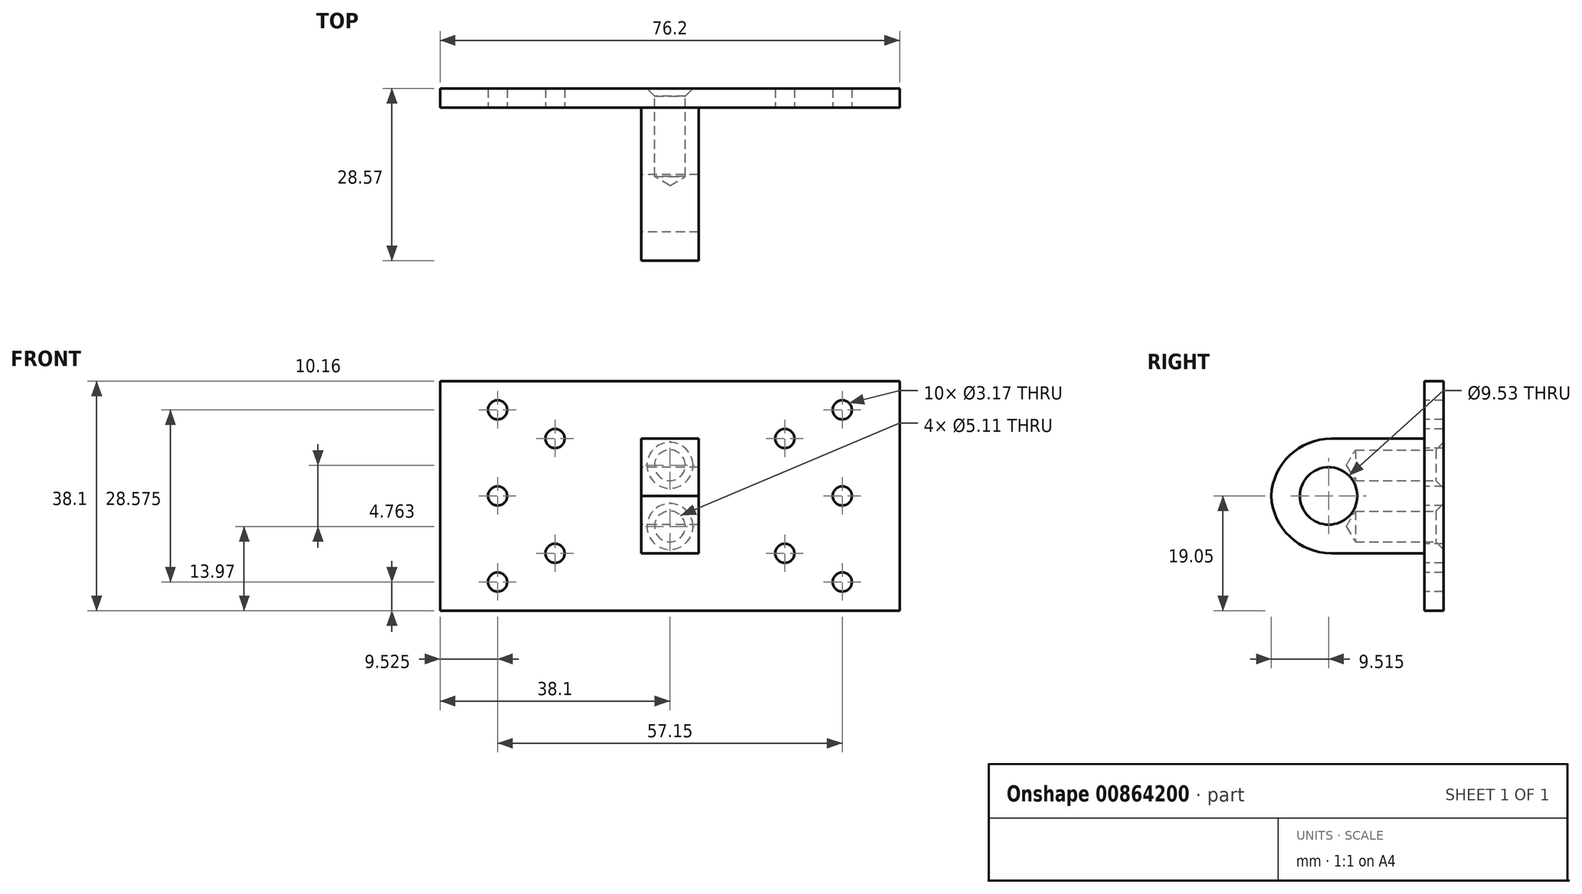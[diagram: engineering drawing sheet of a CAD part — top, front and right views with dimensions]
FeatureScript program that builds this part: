
annotation { "Feature Type Name" : "Feature", "Feature Type Description" : "" }
export const myFeature = defineFeature(function(context is Context, id is Id, definition is map)
    precondition{}
    {
        {
            var Q0;
            Q0=qCreatedBy(makeId("Right.planeOp"),FACE);
            var sketch = newSketch(context, id + "F0", { "sketchPlane" : qUnion([Q0])});
            skLineSegment(sketch, "E0.bottom", {"start": v(-12.7, 9.52) * mm, "end": v(12.7, 9.52) * mm});
            skLineSegment(sketch, "E0.top", {"start": v(-12.7, -9.53) * mm, "end": v(12.7, -9.53) * mm});
            skLineSegment(sketch, "E0.left", {"start": v(-12.7, 9.52) * mm, "end": v(-12.7, -9.53) * mm});
            skLineSegment(sketch, "E0.right", {"start": v(12.7, 9.52) * mm, "end": v(12.7, -9.53) * mm});
            skPoint(sketch, "E0.middle", {"position": v(0, 0) * mm});
            skLineSegment(sketch, "E1", {"start": v(-12.7, 0) * mm, "end": v(-3.18, 0) * mm, "construction": true});
            skPoint(sketch, "E2", {"position": v(-3.18, 0) * mm});
            skCircle(sketch, "E3", {"center": v(-3.18, 0) * mm, "radius": 4.76 * mm});
            skSolve(sketch);
        }
        {
            var Q0;
            Q0=qSketchRegion(id+"F0",true);
            extrude(context, id + "F1", {"entities" : qUnion([Q0]), "endBound" : BoundingType.SYMMETRIC, "depth" : 9.52 * mm, "offsetDistance" : 25.4 * mm});
        }
        {
            var Q0;
            Q0=makeQuery(id+"F1.opExtrude","SWEPT_EDGE",EDGE,{"disambiguationData":[OSD([sQuery(id+"F0.wireOp",EDGE,"E0.bottom"),sQuery(id+"F0.wireOp",EDGE,"E0.left")])]});
            var Q1;
            Q1=makeQuery(id+"F1.opExtrude","SWEPT_EDGE",EDGE,{"disambiguationData":[OSD([sQuery(id+"F0.wireOp",EDGE,"E0.top"),sQuery(id+"F0.wireOp",EDGE,"E0.left")])]});
            fillet(context, id + "F2", {"entities" : qUnion([Q0, Q1]), "radius" : 10 * mm, "tangentPropagation" : true, "allowEdgeOverflow" : false});
        }
        {
            var Q0;
            Q0=makeQuery(id+"F1.opExtrude","SWEPT_FACE",FACE,{"disambiguationData":[OSD([sQuery(id+"F0.wireOp",EDGE,"E0.right")])]});
            var sketch = newSketch(context, id + "F3", { "sketchPlane" : qUnion([Q0])});
            skLineSegment(sketch, "E4.bottom", {"start": v(38.1, -19.05) * mm, "end": v(-38.1, -19.05) * mm});
            skLineSegment(sketch, "E4.top", {"start": v(38.1, 19.05) * mm, "end": v(-38.1, 19.05) * mm});
            skLineSegment(sketch, "E4.left", {"start": v(38.1, -19.05) * mm, "end": v(38.1, 19.05) * mm});
            skLineSegment(sketch, "E4.right", {"start": v(-38.1, -19.05) * mm, "end": v(-38.1, 19.05) * mm});
            skPoint(sketch, "E4.middle", {"position": v(0, 0) * mm});
            skPoint(sketch, "E4.middle.positionSnap0", {"position": v(0, 9.53) * mm});
            skPoint(sketch, "E4.middle.positionSnap1", {"position": v(-4.76, 0) * mm});
            skPoint(sketch, "E4.centerSnap0", {"position": v(0, 9.53) * mm});
            skPoint(sketch, "E4.centerSnap1", {"position": v(-4.76, 0) * mm});
            skLineSegment(sketch, "E5", {"start": v(-38.1, 0) * mm, "end": v(38.1, 0) * mm, "construction": true});
            skLineSegment(sketch, "E6", {"start": v(0, 19.05) * mm, "end": v(0, -19.05) * mm, "construction": true});
            skLineSegment(sketch, "E7", {"start": v(38.1, 19.05) * mm, "end": v(-38.1, -19.05) * mm, "construction": true});
            skLineSegment(sketch, "E8", {"start": v(-38.1, 19.05) * mm, "end": v(38.1, -19.05) * mm, "construction": true});
            skLineSegment(sketch, "E9", {"start": v(-38.1, 19.05) * mm, "end": v(-19.05, 19.05) * mm, "construction": true});
            skLineSegment(sketch, "E10", {"start": v(-19.05, 19.05) * mm, "end": v(-19.05, -23.23) * mm, "construction": true});
            skLineSegment(sketch, "E11", {"start": v(38.1, 19.05) * mm, "end": v(19.05, 19.05) * mm, "construction": true});
            skLineSegment(sketch, "E12", {"start": v(19.05, 19.05) * mm, "end": v(19.05, -31.4) * mm, "construction": true});
            skCircle(sketch, "E13", {"center": v(-19.05, 9.52) * mm, "radius": 1.59 * mm});
            skCircle(sketch, "E14", {"center": v(-19.05, -9.52) * mm, "radius": 1.59 * mm});
            skCircle(sketch, "E15", {"center": v(-28.58, 0) * mm, "radius": 1.59 * mm});
            skPoint(sketch, "E15.centerSnap0", {"position": v(-28.58, 19.05) * mm});
            skCircle(sketch, "E16", {"center": v(-28.58, 14.29) * mm, "radius": 1.59 * mm});
            skCircle(sketch, "E17", {"center": v(-28.58, -14.29) * mm, "radius": 1.59 * mm});
            skPoint(sketch, "E18.MirrorP", {"position": v(28.57, 19.05) * mm});
            skCircle(sketch, "E19.MirrorC", {"center": v(28.58, 14.29) * mm, "radius": 1.59 * mm});
            skCircle(sketch, "E20.MirrorC", {"center": v(28.58, -14.29) * mm, "radius": 1.59 * mm});
            skCircle(sketch, "E21.MirrorC", {"center": v(28.58, 0) * mm, "radius": 1.59 * mm});
            skCircle(sketch, "E22.MirrorC", {"center": v(19.05, -9.52) * mm, "radius": 1.59 * mm});
            skCircle(sketch, "E23.MirrorC", {"center": v(19.05, 9.52) * mm, "radius": 1.59 * mm});
            skSolve(sketch);
        }
        {
            var Q0;
            Q0=makeQuery(id+"F3.imprint","IMPRINT",FACE,{"disambiguationData":[TD([[makeQuery(id+"F3.imprint","IMPRINT",EDGE,{"derivedFrom":sQuery(id+"F3.wireOp",EDGE,"E4.bottom")}),-1.0]])]});
            var Q1;
            {var subQ0=sQuery(id+"F0.wireOp",EDGE,"E0.right");Q1=makeQuery(id+"F3.imprint","IMPRINT",FACE,{"disambiguationData":[TD([[makeQuery(id+"F3.imprint","IMPRINT",EDGE,{"derivedFrom":makeQuery(id+"F1.opExtrude","CAP_EDGE",EDGE,{"disambiguationData":[OSD([subQ0])],"isStart":true})}),-1.0]])]});}
            extrude(context, id + "F4", {"entities" : qUnion([Q0, Q1]), "depth" : 3.17 * mm, "offsetDistance" : 25.4 * mm});
        }
        {
            var Q0;
            Q0=makeQuery(id+"F4.opExtrude","CAP_FACE",FACE,{"disambiguationData":[OSD([sQuery(id+"F3.wireOp",EDGE,"E4.bottom"),sQuery(id+"F3.wireOp",EDGE,"E4.top"),sQuery(id+"F3.wireOp",EDGE,"E4.right"),sQuery(id+"F3.wireOp",EDGE,"E13"),sQuery(id+"F3.wireOp",EDGE,"E14"),sQuery(id+"F3.wireOp",EDGE,"E15"),sQuery(id+"F3.wireOp",EDGE,"E16"),sQuery(id+"F3.wireOp",EDGE,"E17"),sQuery(id+"F3.wireOp",EDGE,"E19.MirrorC"),sQuery(id+"F3.wireOp",EDGE,"E20.MirrorC"),sQuery(id+"F3.wireOp",EDGE,"E21.MirrorC"),sQuery(id+"F3.wireOp",EDGE,"E4.left"),sQuery(id+"F3.wireOp",EDGE,"E22.MirrorC"),sQuery(id+"F3.wireOp",EDGE,"E23.MirrorC")])],"isStart":false});
            var sketch = newSketch(context, id + "F5", { "sketchPlane" : qUnion([Q0])});
            skCircle(sketch, "E24", {"center": v(0, -5.08) * mm, "radius": 1.13 * mm});
            skCircle(sketch, "E25.MirrorC", {"center": v(0, 5.08) * mm, "radius": 1.13 * mm});
            skSolve(sketch);
        }
        {
            var Q0;
            Q0=sQuery(id+"F5.wireOp",VERTEX,"E24.center");
            var Q1;
            Q1=sQuery(id+"F5.wireOp",VERTEX,"E25.MirrorC.center");
            var Q2;
            Q2=makeQuery(id+"F1.opExtrude","SWEPT_BODY",BODY,{"disambiguationData":[OSD([sQuery(id+"F0.wireOp",EDGE,"E0.bottom"),sQuery(id+"F0.wireOp",EDGE,"E0.top"),sQuery(id+"F0.wireOp",EDGE,"E0.left"),sQuery(id+"F0.wireOp",EDGE,"E0.right"),sQuery(id+"F0.wireOp",EDGE,"E3")])]});
            var Q3;
            Q3=makeQuery(id+"F4.opExtrude","SWEPT_BODY",BODY,{"disambiguationData":[OSD([sQuery(id+"F3.wireOp",EDGE,"E4.bottom"),sQuery(id+"F3.wireOp",EDGE,"E4.top"),sQuery(id+"F3.wireOp",EDGE,"E4.right"),sQuery(id+"F3.wireOp",EDGE,"E13"),sQuery(id+"F3.wireOp",EDGE,"E14"),sQuery(id+"F3.wireOp",EDGE,"E15"),sQuery(id+"F3.wireOp",EDGE,"E16"),sQuery(id+"F3.wireOp",EDGE,"E17"),sQuery(id+"F3.wireOp",EDGE,"E19.MirrorC"),sQuery(id+"F3.wireOp",EDGE,"E20.MirrorC"),sQuery(id+"F3.wireOp",EDGE,"E21.MirrorC"),sQuery(id+"F3.wireOp",EDGE,"E4.left"),sQuery(id+"F3.wireOp",EDGE,"E22.MirrorC"),sQuery(id+"F3.wireOp",EDGE,"E23.MirrorC")])]});
            hole(context, id + "F6", {"style" : HoleStyle.C_SINK, "endStyle" : HoleEndStyle.BLIND_IN_LAST, "holeDiameter" : 5.1 * mm, "cSinkDiameter" : 7.62 * mm, "cSinkAngle" : 90 * degree, "tapDrillDiameter" : 5.1 * mm, "majorDiameter" : 6.35 * mm, "holeDepth" : 11.43 * mm, "isTappedThrough" : true, "tappedDepth" : 12.7 * mm, "tapClearance" : 3, "locations" : qUnion([Q0, Q1]), "scope" : qUnion([Q2, Q3])});
        }
    });
